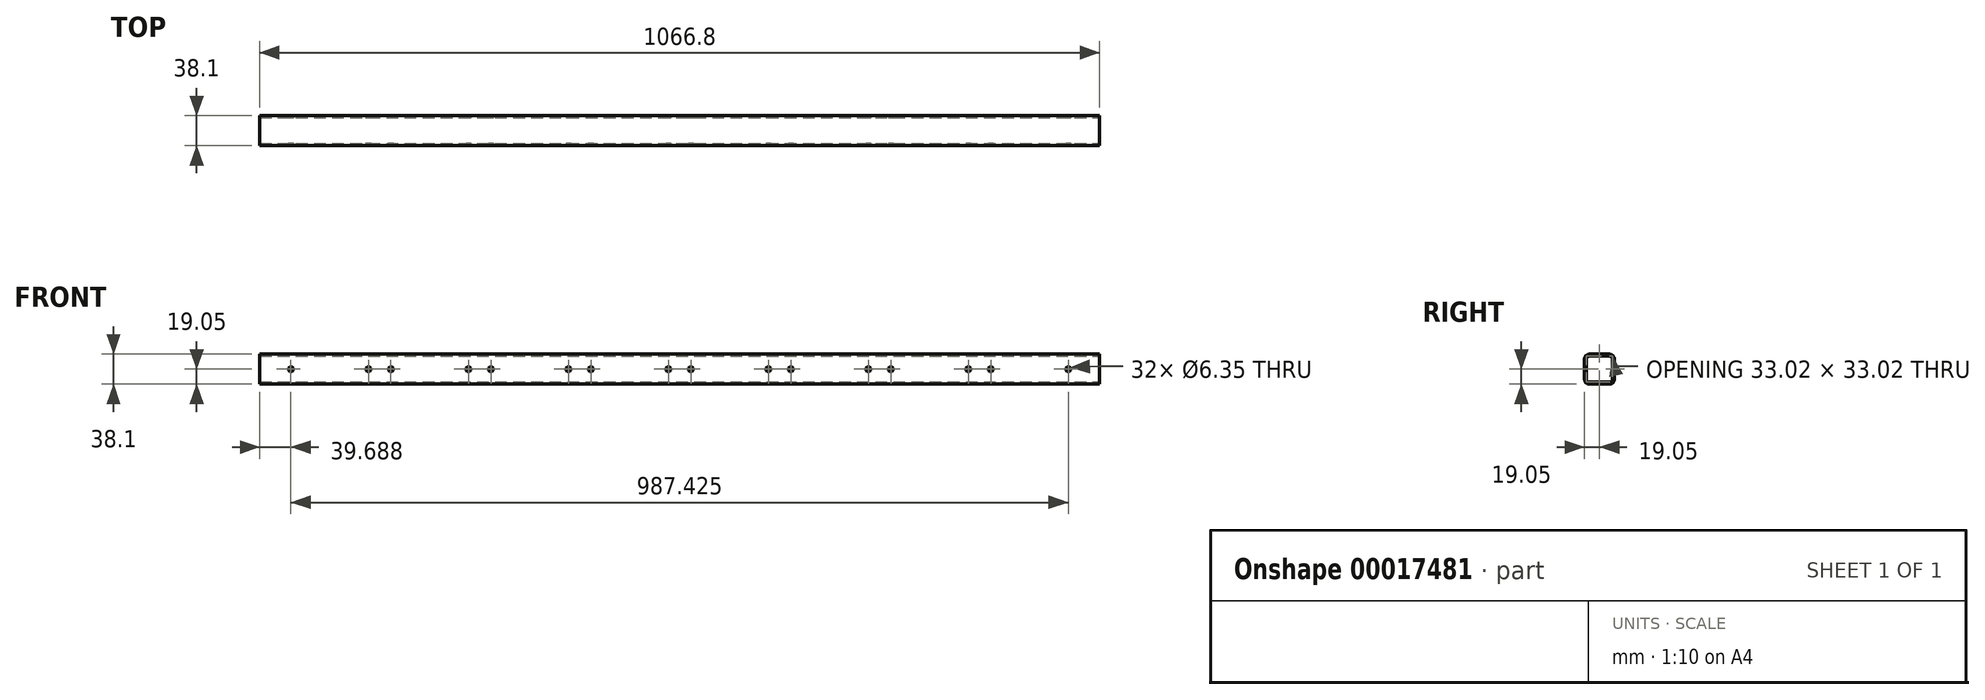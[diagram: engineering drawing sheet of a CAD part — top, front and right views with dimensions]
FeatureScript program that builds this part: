
annotation { "Feature Type Name" : "Feature", "Feature Type Description" : "" }
export const myFeature = defineFeature(function(context is Context, id is Id, definition is map)
    precondition{}
    {
        {
            var Q0;
            Q0=qCreatedBy(makeId("Top.planeOp"),FACE);
            var sketch = newSketch(context, id + "F0", { "sketchPlane" : qUnion([Q0])});
            skLineSegment(sketch, "E0.rect.bottom", {"start": v(533.4, -19.05) * mm, "end": v(-533.4, -19.05) * mm});
            skLineSegment(sketch, "E0.rect.top", {"start": v(533.4, 19.05) * mm, "end": v(-533.4, 19.05) * mm});
            skLineSegment(sketch, "E0.rect.left", {"start": v(533.4, -19.05) * mm, "end": v(533.4, 19.05) * mm});
            skLineSegment(sketch, "E0.rect.right", {"start": v(-533.4, -19.05) * mm, "end": v(-533.4, 19.05) * mm});
            skPoint(sketch, "E0.rect.middle", {"position": v(0, 0) * mm});
            skSolve(sketch);
        }
        {
            var Q0;
            Q0 = qSketchRegion(id + "F0", true);
            extrude(context, id + "F1", {"entities" : qUnion([Q0]), "endBound" : BoundingType.SYMMETRIC, "depth" : 38.1 * mm});
        }
        {
            var Q0;
            Q0=makeQuery(id+"F1.opExtrude","CAP_EDGE",EDGE,{"disambiguationData":[OSD([sQuery(id+"F0.wireOp",EDGE,"E0.rect.bottom")])],"isStart":false});
            var Q1;
            Q1=makeQuery(id+"F1.opExtrude","CAP_EDGE",EDGE,{"disambiguationData":[OSD([sQuery(id+"F0.wireOp",EDGE,"E0.rect.top")])],"isStart":false});
            var Q2;
            Q2=makeQuery(id+"F1.opExtrude","CAP_EDGE",EDGE,{"disambiguationData":[OSD([sQuery(id+"F0.wireOp",EDGE,"E0.rect.bottom")])],"isStart":true});
            var Q3;
            Q3=makeQuery(id+"F1.opExtrude","CAP_EDGE",EDGE,{"disambiguationData":[OSD([sQuery(id+"F0.wireOp",EDGE,"E0.rect.top")])],"isStart":true});
            fillet(context, id + "F2", {"entities" : qUnion([Q0, Q1, Q2, Q3]), "radius" : 6.35 * mm, "tangentPropagation" : true, "allowEdgeOverflow" : false});
        }
        {
            var Q0;
            Q0=makeQuery(id+"F1.opExtrude","SWEPT_FACE",FACE,{"disambiguationData":[OSD([sQuery(id+"F0.wireOp",EDGE,"E0.rect.left")])]});
            var sketch = newSketch(context, id + "F3", { "sketchPlane" : qUnion([Q0])});
            skArc(sketch, "E1.0", {"start": v(-12.7, 16.51) * mm, "mid": v(-15.4, 15.4) * mm, "end": v(-16.51, 12.7) * mm});
            skLineSegment(sketch, "E1.1", {"start": v(-16.5, 12.7) * mm, "end": v(-16.5, -12.7) * mm});
            skArc(sketch, "E1.2", {"start": v(-16.51, -12.7) * mm, "mid": v(-15.4, -15.4) * mm, "end": v(-12.7, -16.51) * mm});
            skLineSegment(sketch, "E1.3", {"start": v(-12.7, -16.51) * mm, "end": v(12.7, -16.51) * mm});
            skArc(sketch, "E1.4", {"start": v(12.7, -16.5) * mm, "mid": v(15.4, -15.4) * mm, "end": v(16.51, -12.7) * mm});
            skLineSegment(sketch, "E1.5", {"start": v(-12.7, 16.51) * mm, "end": v(12.7, 16.51) * mm});
            skLineSegment(sketch, "E1.6", {"start": v(16.51, 12.7) * mm, "end": v(16.51, -12.7) * mm});
            skArc(sketch, "E1.7", {"start": v(16.51, 12.7) * mm, "mid": v(15.4, 15.4) * mm, "end": v(12.7, 16.51) * mm});
            skSolve(sketch);
        }
        {
            var Q0;
            Q0 = qSketchRegion(id + "F3", true);
            extrude(context, id + "F4", {"entities" : qUnion([Q0]), "operationType" : NewBodyOperationType.REMOVE, "endBound" : BoundingType.THROUGH_ALL, "oppositeDirection" : true, "depth" : 25 * mm});
        }
        {
            var Q0;
            Q0=makeQuery(id+"F1.opExtrude","SWEPT_FACE",FACE,{"disambiguationData":[OSD([sQuery(id+"F0.wireOp",EDGE,"E0.rect.bottom")])]});
            var sketch = newSketch(context, id + "F5", { "sketchPlane" : qUnion([Q0])});
            skPoint(sketch, "E2", {"position": v(-493.71, 0) * mm});
            skLineSegment(sketch, "E3", {"start": v(-444.5, 12.7) * mm, "end": v(-444.5, 0) * mm, "construction": true});
            skPoint(sketch, "E4.MirrorP", {"position": v(-395.29, 0) * mm});
            skPoint(sketch, "E5.1.0.0", {"position": v(-268.29, 0) * mm});
            skPoint(sketch, "E5.1.0.1", {"position": v(-366.71, 0) * mm});
            skLineSegment(sketch, "E5.1.0.2", {"start": v(-317.5, 12.7) * mm, "end": v(-317.5, 0) * mm, "construction": true});
            skPoint(sketch, "E5.2.0.0", {"position": v(-141.29, 0) * mm});
            skPoint(sketch, "E5.2.0.1", {"position": v(-239.71, 0) * mm});
            skLineSegment(sketch, "E5.2.0.2", {"start": v(-190.5, 12.7) * mm, "end": v(-190.5, 0) * mm, "construction": true});
            skPoint(sketch, "E5.3.0.0", {"position": v(-14.29, 0) * mm});
            skPoint(sketch, "E5.3.0.1", {"position": v(-112.71, 0) * mm});
            skLineSegment(sketch, "E5.3.0.2", {"start": v(-63.5, 12.7) * mm, "end": v(-63.5, 0) * mm, "construction": true});
            skPoint(sketch, "E5.4.0.0", {"position": v(112.71, 0) * mm});
            skPoint(sketch, "E5.4.0.1", {"position": v(14.29, 0) * mm});
            skLineSegment(sketch, "E5.4.0.2", {"start": v(63.5, 12.7) * mm, "end": v(63.5, 0) * mm, "construction": true});
            skPoint(sketch, "E5.5.0.0", {"position": v(239.71, 0) * mm});
            skPoint(sketch, "E5.5.0.1", {"position": v(141.29, 0) * mm});
            skLineSegment(sketch, "E5.5.0.2", {"start": v(190.5, 12.7) * mm, "end": v(190.5, 0) * mm, "construction": true});
            skPoint(sketch, "E5.6.0.0", {"position": v(366.71, 0) * mm});
            skPoint(sketch, "E5.6.0.1", {"position": v(268.29, 0) * mm});
            skLineSegment(sketch, "E5.6.0.2", {"start": v(317.5, 12.7) * mm, "end": v(317.5, 0) * mm, "construction": true});
            skPoint(sketch, "E5.7.0.0", {"position": v(493.71, 0) * mm});
            skPoint(sketch, "E5.7.0.1", {"position": v(395.29, 0) * mm});
            skLineSegment(sketch, "E5.7.0.2", {"start": v(444.5, 12.7) * mm, "end": v(444.5, 0) * mm, "construction": true});
            skLineSegment(sketch, "E5.direction1", {"start": v(-395.29, 0) * mm, "end": v(-268.29, 0) * mm, "construction": true});
            skLineSegment(sketch, "E6", {"start": v(-493.71, 0) * mm, "end": v(-533.4, 0) * mm, "construction": true});
            skLineSegment(sketch, "E7", {"start": v(493.71, 0) * mm, "end": v(533.4, 0) * mm, "construction": true});
            skSolve(sketch);
        }
        {
            var Q0;
            Q0=sQuery(id+"F5.wireOp",VERTEX,"E2");
            var Q1;
            Q1=sQuery(id+"F5.wireOp",VERTEX,"E4.MirrorP");
            var Q2;
            Q2=sQuery(id+"F5.wireOp",VERTEX,"E5.1.0.1");
            var Q3;
            Q3=sQuery(id+"F5.wireOp",VERTEX,"E5.1.0.0");
            var Q4;
            Q4=sQuery(id+"F5.wireOp",VERTEX,"E5.2.0.1");
            var Q5;
            Q5=sQuery(id+"F5.wireOp",VERTEX,"E5.2.0.0");
            var Q6;
            Q6=sQuery(id+"F5.wireOp",VERTEX,"E5.3.0.1");
            var Q7;
            Q7=sQuery(id+"F5.wireOp",VERTEX,"E5.3.0.0");
            var Q8;
            Q8=sQuery(id+"F5.wireOp",VERTEX,"E5.4.0.1");
            var Q9;
            Q9=sQuery(id+"F5.wireOp",VERTEX,"E5.4.0.0");
            var Q10;
            Q10=sQuery(id+"F5.wireOp",VERTEX,"E5.5.0.1");
            var Q11;
            Q11=sQuery(id+"F5.wireOp",VERTEX,"E5.5.0.0");
            var Q12;
            Q12=sQuery(id+"F5.wireOp",VERTEX,"E5.6.0.1");
            var Q13;
            Q13=sQuery(id+"F5.wireOp",VERTEX,"E5.6.0.0");
            var Q14;
            Q14=sQuery(id+"F5.wireOp",VERTEX,"E5.7.0.1");
            var Q15;
            Q15=sQuery(id+"F5.wireOp",VERTEX,"E5.7.0.0");
            var Q16;
            Q16=makeQuery(id+"F1.opExtrude","SWEPT_BODY",BODY,{"disambiguationData":[OSD([sQuery(id+"F0.wireOp",EDGE,"E0.rect.bottom"),sQuery(id+"F0.wireOp",EDGE,"E0.rect.top"),sQuery(id+"F0.wireOp",EDGE,"E0.rect.left"),sQuery(id+"F0.wireOp",EDGE,"E0.rect.right")])]});
            hole(context, id + "F6", {"style" : HoleStyle.SIMPLE, "holeDiameter" : 6.35 * mm, "endStyle" : HoleEndStyle.THROUGH, "locations" : qUnion([Q0, Q1, Q2, Q3, Q4, Q5, Q6, Q7, Q8, Q9, Q10, Q11, Q12, Q13, Q14, Q15]), "scope" : qUnion([Q16])});
        }
    });
